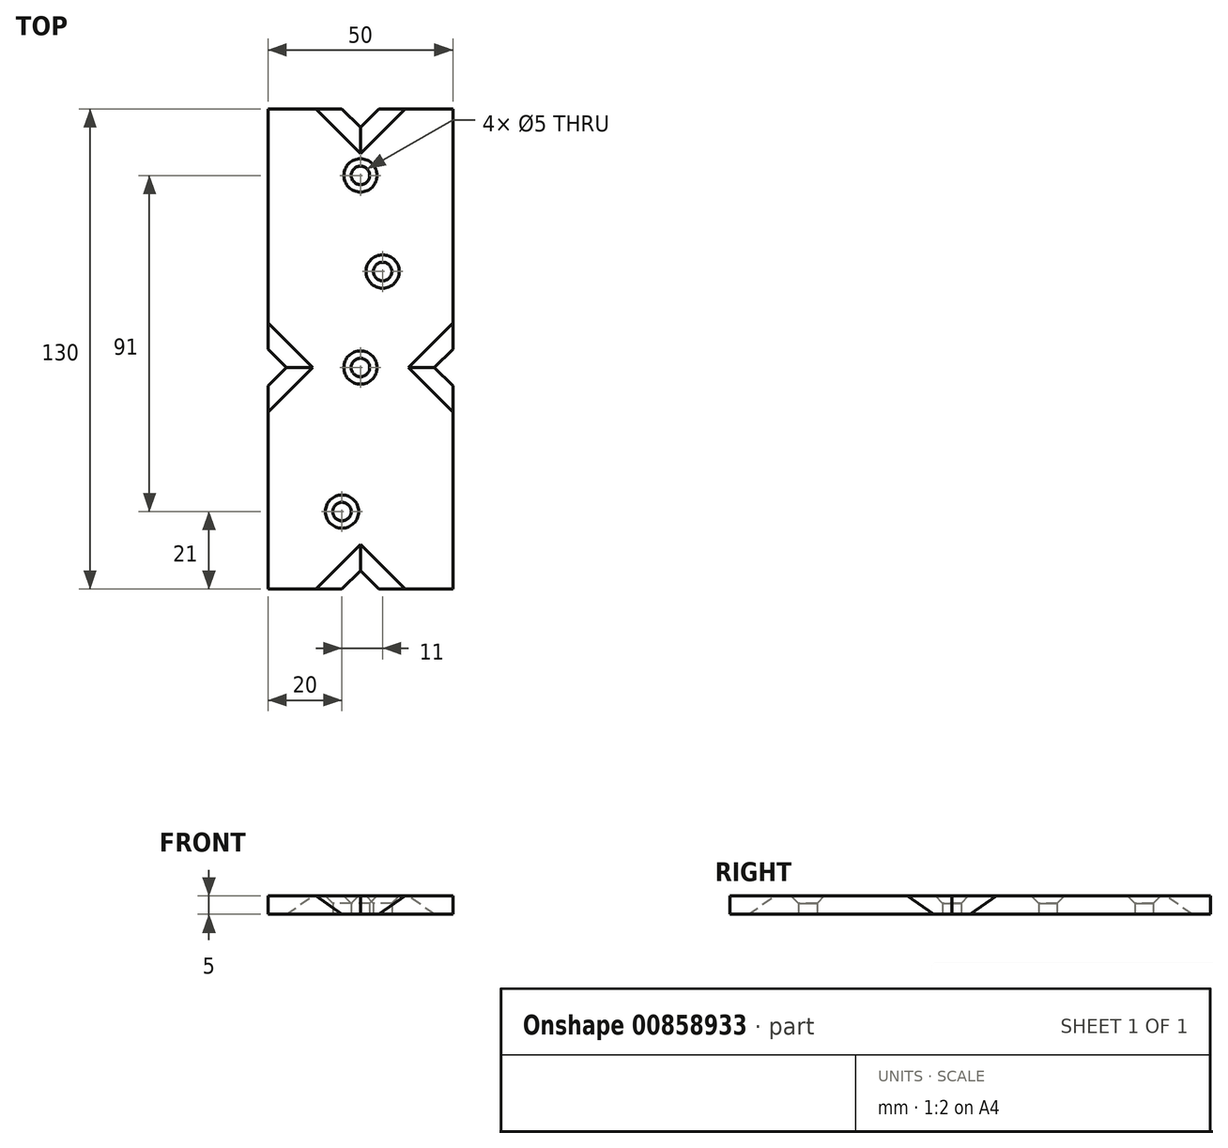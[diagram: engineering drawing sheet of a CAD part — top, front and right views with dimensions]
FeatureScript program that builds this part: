
annotation { "Feature Type Name" : "Feature", "Feature Type Description" : "" }
export const myFeature = defineFeature(function(context is Context, id is Id, definition is map)
    precondition{}
    {
        {
            var Q0;
            Q0=qCreatedBy(makeId("Top.planeOp"),FACE);
            var sketch = newSketch(context, id + "F0", { "sketchPlane" : qUnion([Q0])});
            skCircle(sketch, "E0", {"center": v(-5, -39) * mm, "radius": 2.5 * mm});
            skCircle(sketch, "E1", {"center": v(0, 0) * mm, "radius": 2.5 * mm});
            skCircle(sketch, "E2", {"center": v(6, 26) * mm, "radius": 2.5 * mm});
            skCircle(sketch, "E3", {"center": v(0, 52) * mm, "radius": 2.5 * mm});
            skLineSegment(sketch, "E4.bottom", {"start": v(-25, 70) * mm, "end": v(25, 70) * mm});
            skLineSegment(sketch, "E4.top", {"start": v(-25, -60) * mm, "end": v(25, -60) * mm});
            skLineSegment(sketch, "E4.left", {"start": v(-25, 70) * mm, "end": v(-25, -60) * mm});
            skLineSegment(sketch, "E4.right", {"start": v(25, 70) * mm, "end": v(25, -60) * mm});
            skLineSegment(sketch, "E5", {"start": v(-25, 5) * mm, "end": v(-20, 0) * mm});
            skLineSegment(sketch, "E6", {"start": v(-20, 0) * mm, "end": v(-25, -5) * mm});
            skLineSegment(sketch, "E7", {"start": v(-25, -5) * mm, "end": v(-25, 5) * mm});
            skLineSegment(sketch, "E8", {"start": v(25, 5) * mm, "end": v(20, 0) * mm});
            skLineSegment(sketch, "E9", {"start": v(20, 0) * mm, "end": v(25, -5) * mm});
            skLineSegment(sketch, "E10", {"start": v(25, -5) * mm, "end": v(25, 5) * mm});
            skLineSegment(sketch, "E11", {"start": v(-5, -60) * mm, "end": v(0, -55) * mm});
            skLineSegment(sketch, "E12", {"start": v(0, -55) * mm, "end": v(5, -60) * mm});
            skLineSegment(sketch, "E13", {"start": v(5, -60) * mm, "end": v(-5, -60) * mm});
            skLineSegment(sketch, "E14", {"start": v(-5, 70) * mm, "end": v(5, 70) * mm});
            skLineSegment(sketch, "E15", {"start": v(5, 70) * mm, "end": v(0, 65) * mm});
            skLineSegment(sketch, "E16", {"start": v(0, 65) * mm, "end": v(-5, 70) * mm});
            skSolve(sketch);
        }
        {
            var Q0;
            Q0=makeQuery(id+"F0.imprint","IMPRINT",FACE,{"disambiguationData":[TD([[makeQuery(id+"F0.imprint","IMPRINT",EDGE,{"derivedFrom":sQuery(id+"F0.wireOp",EDGE,"E0")}),-1.0]])]});
            extrude(context, id + "F1", {"entities" : qUnion([Q0]), "depth" : 5 * mm, "offsetDistance" : 25 * mm});
        }
        {
            var Q0;
            Q0=makeQuery(id+"F1.opExtrude","CAP_EDGE",EDGE,{"disambiguationData":[OSD([sQuery(id+"F0.wireOp",EDGE,"E16")])],"isStart":false});
            var Q1;
            Q1=makeQuery(id+"F1.opExtrude","CAP_EDGE",EDGE,{"disambiguationData":[OSD([sQuery(id+"F0.wireOp",EDGE,"E15")])],"isStart":false});
            var Q2;
            Q2=makeQuery(id+"F1.opExtrude","CAP_EDGE",EDGE,{"disambiguationData":[OSD([sQuery(id+"F0.wireOp",EDGE,"E8")])],"isStart":false});
            var Q3;
            Q3=makeQuery(id+"F1.opExtrude","CAP_EDGE",EDGE,{"disambiguationData":[OSD([sQuery(id+"F0.wireOp",EDGE,"E9")])],"isStart":false});
            var Q4;
            Q4=makeQuery(id+"F1.opExtrude","CAP_EDGE",EDGE,{"disambiguationData":[OSD([sQuery(id+"F0.wireOp",EDGE,"E5")])],"isStart":false});
            var Q5;
            Q5=makeQuery(id+"F1.opExtrude","CAP_EDGE",EDGE,{"disambiguationData":[OSD([sQuery(id+"F0.wireOp",EDGE,"E6")])],"isStart":false});
            var Q6;
            Q6=makeQuery(id+"F1.opExtrude","CAP_EDGE",EDGE,{"disambiguationData":[OSD([sQuery(id+"F0.wireOp",EDGE,"E11")])],"isStart":false});
            var Q7;
            Q7=makeQuery(id+"F1.opExtrude","CAP_EDGE",EDGE,{"disambiguationData":[OSD([sQuery(id+"F0.wireOp",EDGE,"E12")])],"isStart":false});
            chamfer(context, id + "F2", {"entities" : qUnion([Q0, Q1, Q2, Q3, Q4, Q5, Q6, Q7]), "width" : 5 * mm, "tangentPropagation" : true});
        }
        {
            var Q0;
            Q0=makeQuery(id+"F1.opExtrude","CAP_EDGE",EDGE,{"disambiguationData":[OSD([sQuery(id+"F0.wireOp",EDGE,"E3")])],"isStart":false});
            var Q1;
            Q1=makeQuery(id+"F1.opExtrude","CAP_EDGE",EDGE,{"disambiguationData":[OSD([sQuery(id+"F0.wireOp",EDGE,"E2")])],"isStart":false});
            var Q2;
            Q2=makeQuery(id+"F1.opExtrude","CAP_EDGE",EDGE,{"disambiguationData":[OSD([sQuery(id+"F0.wireOp",EDGE,"E0")])],"isStart":false});
            var Q3;
            Q3=makeQuery(id+"F1.opExtrude","CAP_EDGE",EDGE,{"disambiguationData":[OSD([sQuery(id+"F0.wireOp",EDGE,"E1")])],"isStart":false});
            chamfer(context, id + "F3", {"entities" : qUnion([Q0, Q1, Q2, Q3]), "width" : 2 * mm, "tangentPropagation" : true});
        }
    });
